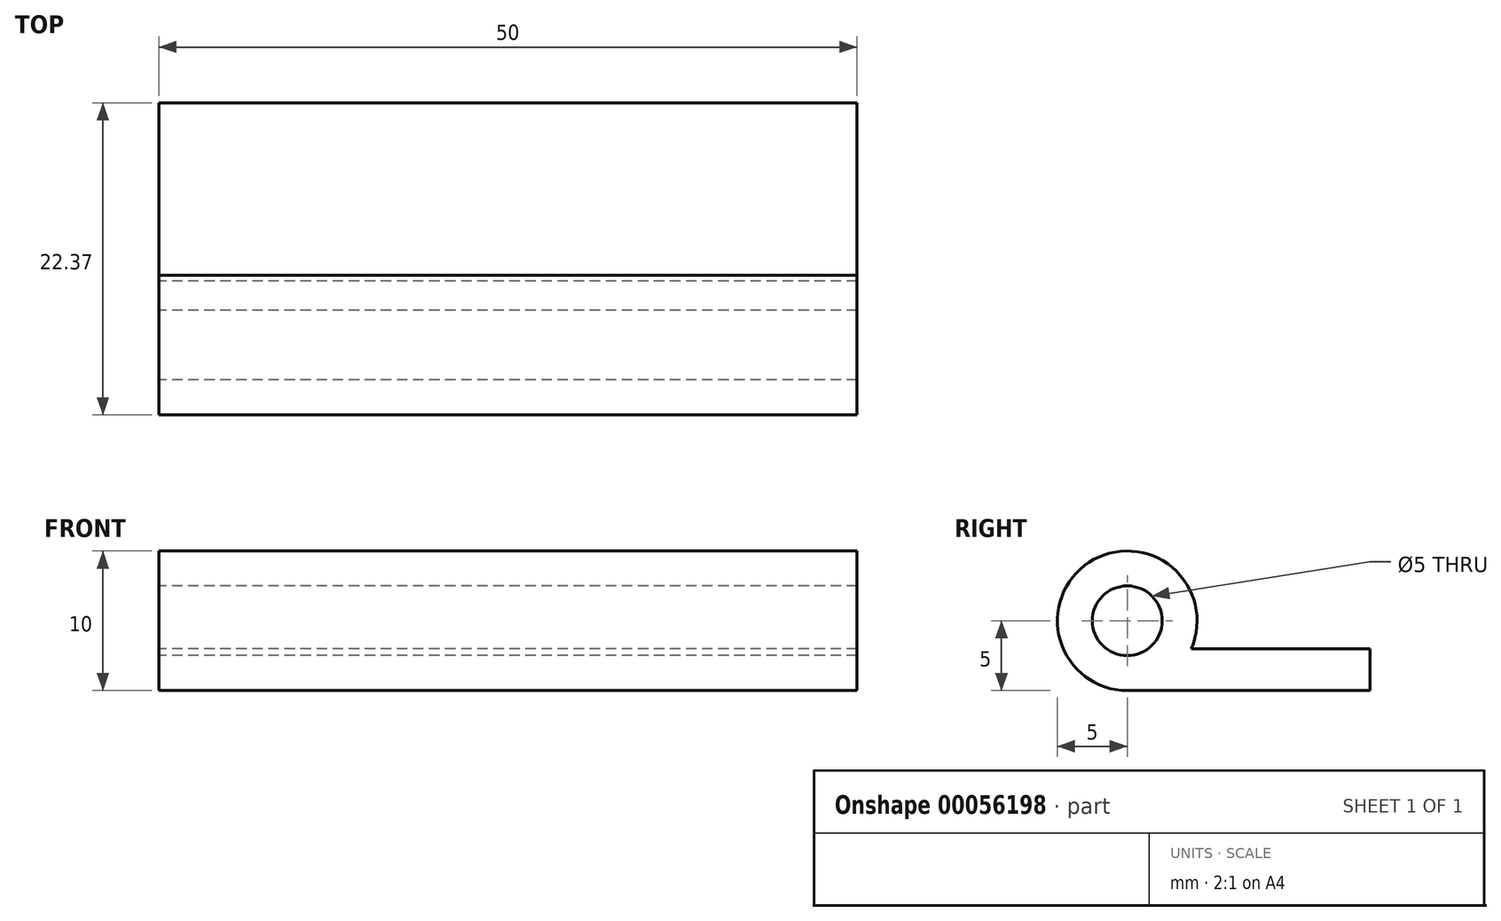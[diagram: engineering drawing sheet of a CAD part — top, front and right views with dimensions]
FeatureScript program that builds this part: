
annotation { "Feature Type Name" : "Feature", "Feature Type Description" : "" }
export const myFeature = defineFeature(function(context is Context, id is Id, definition is map)
    precondition{}
    {
        {
            var Q0;
            Q0=qCreatedBy(makeId("Right.planeOp"),FACE);
            var sketch = newSketch(context, id + "F0", { "sketchPlane" : qUnion([Q0])});
            skArc(sketch, "E0", {"start": v(4.58, -2) * mm, "mid": v(-2.74, 4.18) * mm, "end": v(0, -5) * mm});
            skLineSegment(sketch, "E1.bottom", {"start": v(0, -5) * mm, "end": v(17.37, -5) * mm});
            skLineSegment(sketch, "E1.top", {"start": v(4.58, -2) * mm, "end": v(17.37, -2) * mm});
            skLineSegment(sketch, "E1.right", {"start": v(17.37, -5) * mm, "end": v(17.37, -2) * mm});
            skCircle(sketch, "E2", {"center": v(0, 0) * mm, "radius": 2.5 * mm});
            skSolve(sketch);
        }
        {
            var Q0;
            Q0=makeQuery(id+"F0.imprint","IMPRINT",FACE,{"disambiguationData":[TD([[makeQuery(id+"F0.imprint","IMPRINT",EDGE,{"derivedFrom":sQuery(id+"F0.wireOp",EDGE,"E0")}),1.0]])]});
            extrude(context, id + "F1", {"entities" : qUnion([Q0]), "depth" : 50 * mm});
        }
    });
